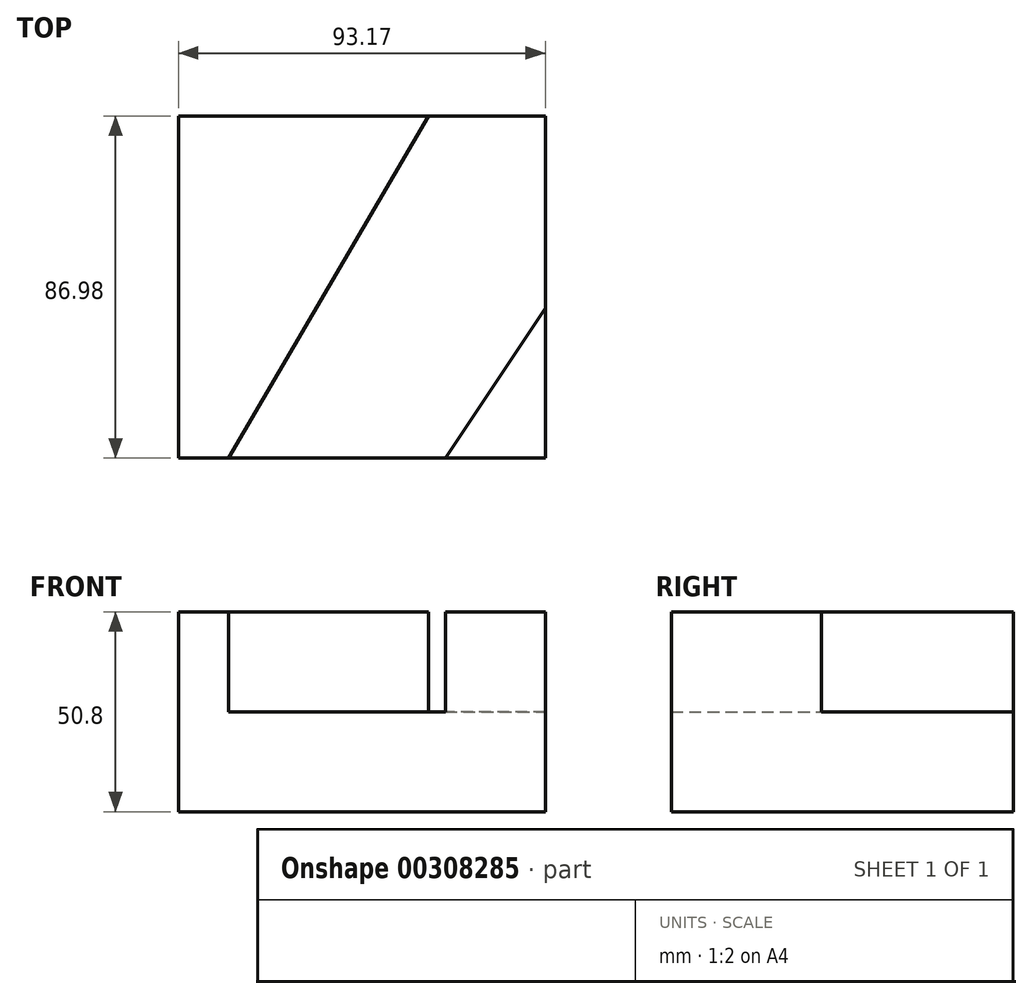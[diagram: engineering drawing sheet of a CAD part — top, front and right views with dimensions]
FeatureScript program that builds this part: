
annotation { "Feature Type Name" : "Feature", "Feature Type Description" : "" }
export const myFeature = defineFeature(function(context is Context, id is Id, definition is map)
    precondition{}
    {
        {
            var Q0;
            Q0=qCreatedBy(makeId("Top.planeOp"),FACE);
            var sketch = newSketch(context, id + "F0", { "sketchPlane" : qUnion([Q0])});
            skLineSegment(sketch, "E0", {"start": v(-51.7, 46.58) * mm, "end": v(-51.7, -40.4) * mm});
            skLineSegment(sketch, "E1", {"start": v(-51.7, -40.4) * mm, "end": v(41.48, -40.4) * mm});
            skLineSegment(sketch, "E2", {"start": v(41.48, -40.4) * mm, "end": v(41.48, 46.58) * mm});
            skLineSegment(sketch, "E3", {"start": v(41.48, 46.58) * mm, "end": v(-51.7, 46.58) * mm});
            skSolve(sketch);
        }
        {
            var Q0;
            Q0 = qSketchRegion(id + "F0", true);
            extrude(context, id + "F1", {"entities" : qUnion([Q0]), "depth" : 25.4 * mm});
        }
        {
            var Q0;
            Q0=makeQuery(id+"F1.opExtrude","CAP_FACE",FACE,{"disambiguationData":[OSD([sQuery(id+"F0.wireOp",EDGE,"E0"),sQuery(id+"F0.wireOp",EDGE,"E1"),sQuery(id+"F0.wireOp",EDGE,"E2"),sQuery(id+"F0.wireOp",EDGE,"E3")])],"isStart":false});
            var sketch = newSketch(context, id + "F2", { "sketchPlane" : qUnion([Q0])});
            skLineSegment(sketch, "E4", {"start": v(-39, -40.4) * mm, "end": v(11.8, 46.58) * mm});
            skLineSegment(sketch, "E5", {"start": v(16.08, -40.4) * mm, "end": v(41.48, -2.3) * mm});
            skLineSegment(sketch, "E6", {"start": v(16.08, -40.4) * mm, "end": v(41.48, -40.4) * mm});
            skLineSegment(sketch, "E7", {"start": v(41.48, -2.3) * mm, "end": v(41.48, -40.4) * mm});
            skLineSegment(sketch, "E8", {"start": v(-39, -40.4) * mm, "end": v(-51.7, -40.4) * mm});
            skLineSegment(sketch, "E9", {"start": v(-51.7, 46.58) * mm, "end": v(11.8, 46.58) * mm});
            skSolve(sketch);
        }
        {
            var Q0;
            Q0=makeQuery(id+"F2.imprint","IMPRINT",FACE,{"disambiguationData":[TD([[makeQuery(id+"F2.imprint","IMPRINT",EDGE,{"derivedFrom":sQuery(id+"F2.wireOp",EDGE,"E5")}),-1.0]])]});
            var Q1;
            Q1=makeQuery(id+"F2.imprint","IMPRINT",FACE,{"disambiguationData":[TD([[makeQuery(id+"F2.imprint","IMPRINT",EDGE,{"derivedFrom":sQuery(id+"F2.wireOp",EDGE,"E4")}),1.0]])]});
            extrude(context, id + "F3", {"entities" : qUnion([Q0, Q1]), "operationType" : NewBodyOperationType.ADD, "depth" : 25.4 * mm});
        }
    });
